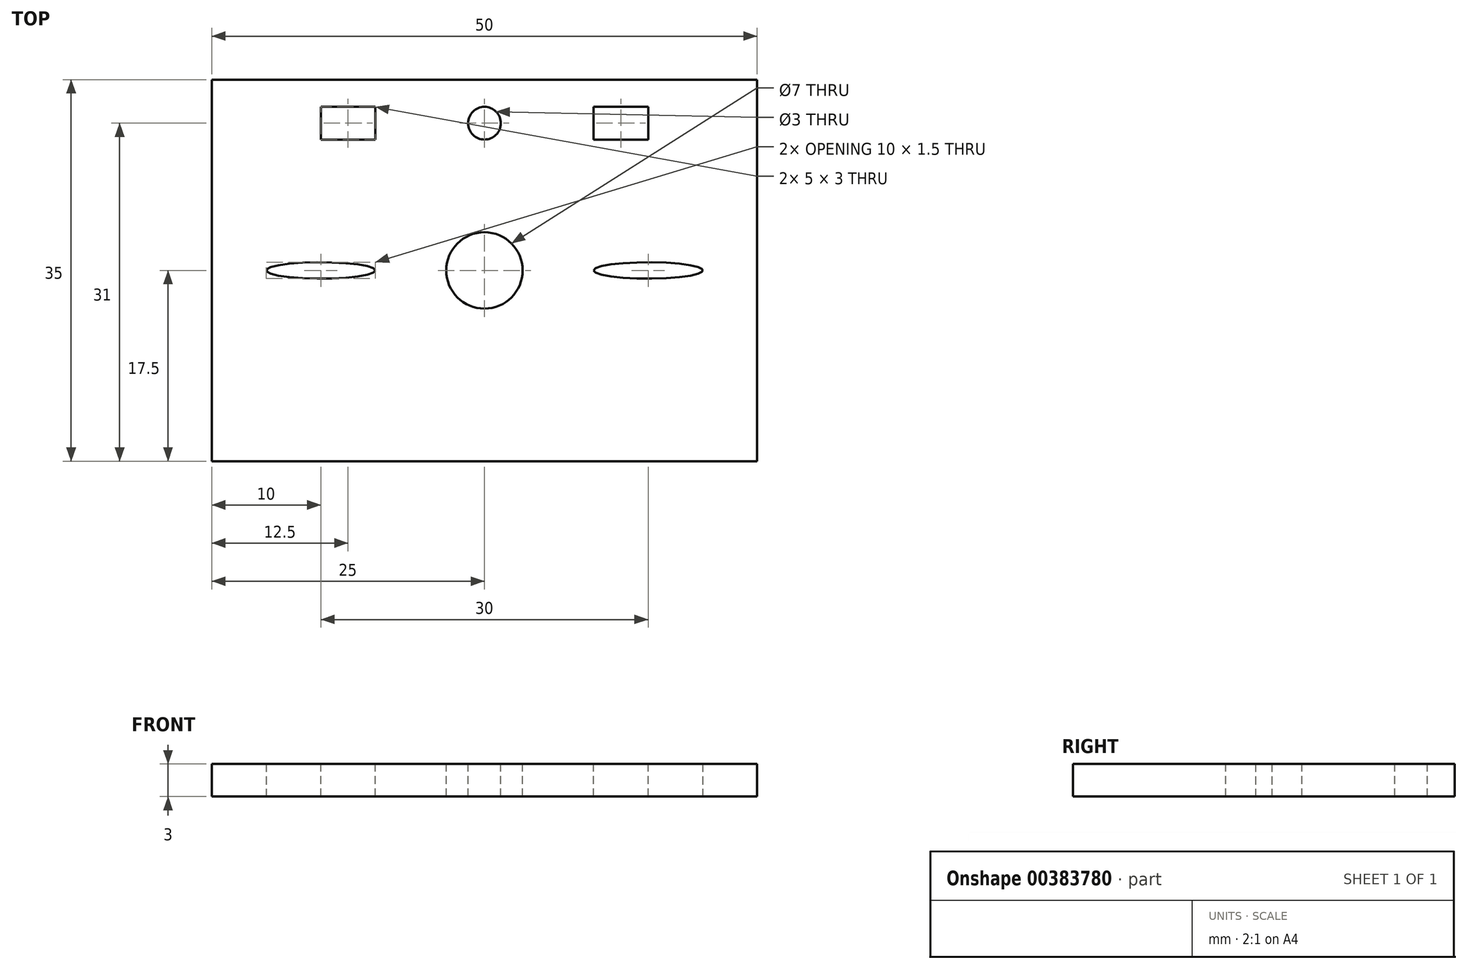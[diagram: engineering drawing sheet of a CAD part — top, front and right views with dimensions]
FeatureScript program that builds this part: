
annotation { "Feature Type Name" : "Feature", "Feature Type Description" : "" }
export const myFeature = defineFeature(function(context is Context, id is Id, definition is map)
    precondition{}
    {
        {
            var Q0;
            Q0=qCreatedBy(makeId("Top.planeOp"),FACE);
            var sketch = newSketch(context, id + "F0", { "sketchPlane" : qUnion([Q0])});
            skLineSegment(sketch, "E0.bottom", {"start": v(25, 17.5) * mm, "end": v(-25, 17.5) * mm});
            skLineSegment(sketch, "E0.top", {"start": v(25, -17.5) * mm, "end": v(-25, -17.5) * mm});
            skLineSegment(sketch, "E0.left", {"start": v(25, 17.5) * mm, "end": v(25, -17.5) * mm});
            skLineSegment(sketch, "E0.right", {"start": v(-25, 17.5) * mm, "end": v(-25, -17.5) * mm});
            skPoint(sketch, "E0.middle", {"position": v(0, 0) * mm});
            skSolve(sketch);
        }
        {
            var Q0;
            Q0 = qSketchRegion(id + "F0", true);
            extrude(context, id + "F1", {"entities" : qUnion([Q0]), "depth" : 3 * mm});
        }
        {
            var Q0;
            Q0=makeQuery(id+"F1.opExtrude","CAP_FACE",FACE,{"disambiguationData":[OSD([sQuery(id+"F0.wireOp",EDGE,"E0.bottom"),sQuery(id+"F0.wireOp",EDGE,"E0.top"),sQuery(id+"F0.wireOp",EDGE,"E0.left"),sQuery(id+"F0.wireOp",EDGE,"E0.right")])],"isStart":false});
            var sketch = newSketch(context, id + "F2", { "sketchPlane" : qUnion([Q0])});
            skLineSegment(sketch, "E1.bottom", {"start": v(-10, 12) * mm, "end": v(-15, 12) * mm});
            skLineSegment(sketch, "E1.top", {"start": v(-10, 15) * mm, "end": v(-15, 15) * mm});
            skLineSegment(sketch, "E1.left", {"start": v(-10, 12) * mm, "end": v(-10, 15) * mm});
            skLineSegment(sketch, "E1.right", {"start": v(-15, 12) * mm, "end": v(-15, 15) * mm});
            skPoint(sketch, "E1.middle", {"position": v(-12.5, 13.5) * mm});
            skLineSegment(sketch, "E2.MirrorCS", {"start": v(15, 12) * mm, "end": v(15, 15) * mm});
            skLineSegment(sketch, "E3.MirrorCS", {"start": v(10, 12) * mm, "end": v(10, 15) * mm});
            skLineSegment(sketch, "E4.MirrorCS", {"start": v(10, 12) * mm, "end": v(15, 12) * mm});
            skLineSegment(sketch, "E5.MirrorCS", {"start": v(10, 15) * mm, "end": v(15, 15) * mm});
            skPoint(sketch, "E6.MirrorP", {"position": v(12.5, 13.5) * mm});
            skCircle(sketch, "E7", {"center": v(0, 0) * mm, "radius": 3.5 * mm});
            skCircle(sketch, "E8", {"center": v(0, 13.5) * mm, "radius": 1.5 * mm});
            skLineSegment(sketch, "E9", {"start": v(-12.5, 13.5) * mm, "end": v(12.5, 13.5) * mm, "construction": true});
            skEllipse(sketch, "E10", {"center": v(-15, 0) * mm, "majorRadius": 5 * mm, "minorRadius": 0.75 * mm, "majorAxis": v(1, 0)});
            skEllipse(sketch, "E11.MirrorC", {"center": v(15, 0) * mm, "majorRadius": 5 * mm, "minorRadius": 0.75 * mm, "majorAxis": v(-1, 0)});
            skSolve(sketch);
        }
        {
            var Q0;
            Q0 = qSketchRegion(id + "F2", true);
            extrude(context, id + "F3", {"entities" : qUnion([Q0]), "operationType" : NewBodyOperationType.REMOVE, "oppositeDirection" : true, "depth" : 25 * mm});
        }
    });
